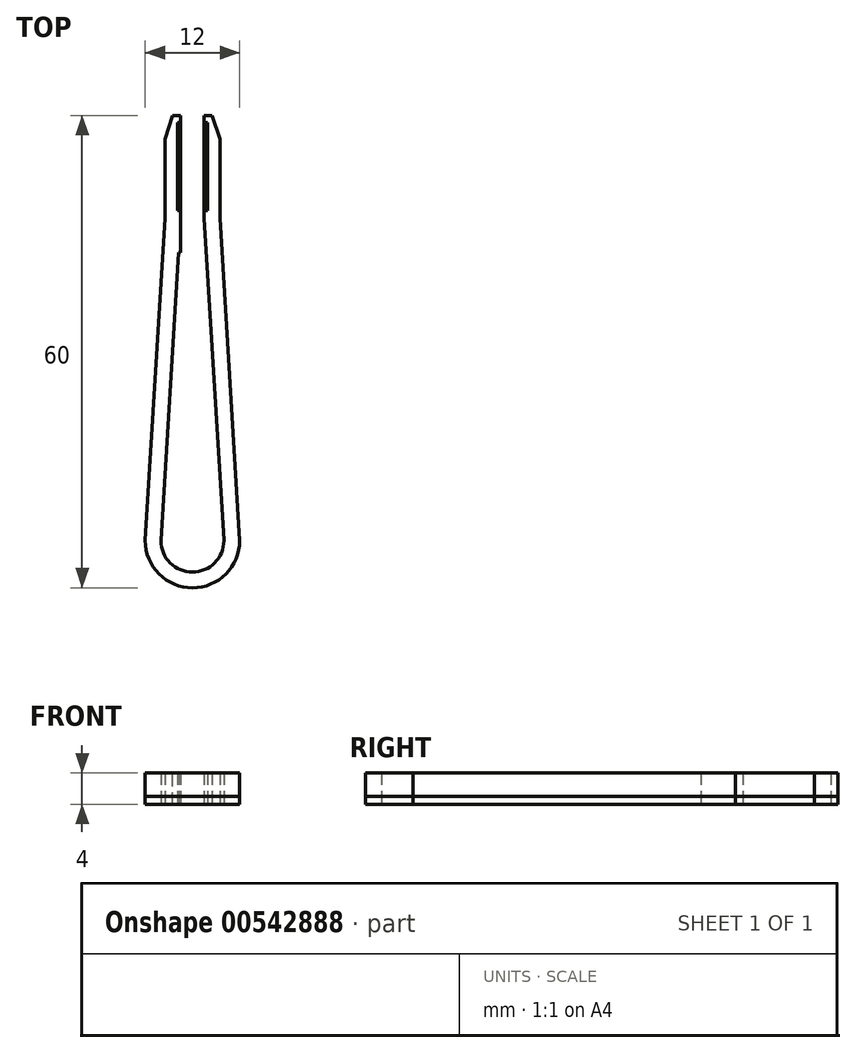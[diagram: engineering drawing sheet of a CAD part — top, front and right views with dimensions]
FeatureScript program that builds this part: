
annotation { "Feature Type Name" : "Feature", "Feature Type Description" : "" }
export const myFeature = defineFeature(function(context is Context, id is Id, definition is map)
    precondition{}
    {
        {
            var Q0;
            Q0=qCreatedBy(makeId("Top.planeOp"),FACE);
            var sketch = newSketch(context, id + "F0", { "sketchPlane" : qUnion([Q0])});
            skArc(sketch, "E0", {"start": v(-4, 0) * mm, "mid": v(0, -4) * mm, "end": v(4, 0) * mm});
            skArc(sketch, "E1", {"start": v(-6, 0) * mm, "mid": v(0, -6) * mm, "end": v(6, 0) * mm});
            skLineSegment(sketch, "E2.top", {"start": v(-1.5, 54) * mm, "end": v(-3.5, 54) * mm});
            skLineSegment(sketch, "E2.left", {"start": v(-1.5, 41.9) * mm, "end": v(-1.5, 54) * mm});
            skLineSegment(sketch, "E2.right", {"start": v(-3.5, 41) * mm, "end": v(-3.5, 54) * mm});
            skLineSegment(sketch, "E3.top", {"start": v(3.5, 54) * mm, "end": v(1.5, 54) * mm});
            skLineSegment(sketch, "E3.left", {"start": v(3.5, 41) * mm, "end": v(3.5, 54) * mm});
            skLineSegment(sketch, "E3.right", {"start": v(1.5, 41) * mm, "end": v(1.5, 54) * mm});
            skPoint(sketch, "E4", {"position": v(1.5, 47.5) * mm});
            skLineSegment(sketch, "E5.bottom", {"start": v(1.9, 53.1) * mm, "end": v(1.5, 53.1) * mm});
            skLineSegment(sketch, "E5.top", {"start": v(1.9, 41.9) * mm, "end": v(1.5, 41.9) * mm});
            skLineSegment(sketch, "E5.left", {"start": v(1.9, 53.1) * mm, "end": v(1.9, 41.9) * mm});
            skLineSegment(sketch, "E6", {"start": v(3.5, 41) * mm, "end": v(6, 0) * mm});
            skLineSegment(sketch, "E7", {"start": v(-3.5, 41) * mm, "end": v(-6, 0) * mm});
            skLineSegment(sketch, "E8", {"start": v(-1.77, 36.6) * mm, "end": v(-4, 0) * mm});
            skLineSegment(sketch, "E9", {"start": v(4, 0) * mm, "end": v(1.5, 41) * mm});
            skLineSegment(sketch, "E10.bottom", {"start": v(-1.5, 53.1) * mm, "end": v(-1.9, 53.1) * mm});
            skLineSegment(sketch, "E10.top", {"start": v(-1.5, 41.9) * mm, "end": v(-1.9, 41.9) * mm});
            skLineSegment(sketch, "E10.right", {"start": v(-1.9, 53.1) * mm, "end": v(-1.9, 41.9) * mm});
            skPoint(sketch, "E10.middle", {"position": v(-1.5, 47.3) * mm});
            skLineSegment(sketch, "E11", {"start": v(-1.5, 36.59) * mm, "end": v(-1.77, 36.6) * mm});
            skLineSegment(sketch, "E12", {"start": v(-1.5, 41.9) * mm, "end": v(-1.5, 36.59) * mm});
            skSolve(sketch);
        }
        {
            var Q0;
            Q0 = qSketchRegion(id + "F0", true);
            extrude(context, id + "F1", {"entities" : qUnion([Q0]), "depth" : 1 * mm, "offsetDistance" : 25 * mm});
        }
        {
            var Q0;
            Q0=makeQuery(id+"F0.imprint","IMPRINT",FACE,{"disambiguationData":[TD([[makeQuery(id+"F0.imprint","IMPRINT",EDGE,{"derivedFrom":sQuery(id+"F0.wireOp",EDGE,"E0")}),-1.0]])]});
            extrude(context, id + "F2", {"entities" : qUnion([Q0]), "depth" : 4 * mm, "offsetDistance" : 25 * mm});
        }
        {
            var Q0;
            Q0=makeQuery(id+"F2.opExtrude","SWEPT_EDGE",EDGE,{"disambiguationData":[OSD([sQuery(id+"F0.wireOp",EDGE,"E2.top"),sQuery(id+"F0.wireOp",EDGE,"E2.right")])]});
            var Q1;
            Q1=makeQuery(id+"F1.opExtrude","SWEPT_EDGE",EDGE,{"disambiguationData":[OSD([sQuery(id+"F0.wireOp",EDGE,"E2.top"),sQuery(id+"F0.wireOp",EDGE,"E2.right")])]});
            chamfer(context, id + "F3", {"entities" : qUnion([Q0, Q1]), "chamferType" : ChamferType.TWO_OFFSETS, "width1" : 3 * mm, "oppositeDirection" : false, "width2" : 1 * mm, "tangentPropagation" : true});
        }
        {
            var Q0;
            Q0=makeQuery(id+"F1.opExtrude","SWEPT_EDGE",EDGE,{"disambiguationData":[OSD([sQuery(id+"F0.wireOp",EDGE,"E3.top"),sQuery(id+"F0.wireOp",EDGE,"E3.left")])]});
            var Q1;
            Q1=makeQuery(id+"F2.opExtrude","SWEPT_EDGE",EDGE,{"disambiguationData":[OSD([sQuery(id+"F0.wireOp",EDGE,"E3.top"),sQuery(id+"F0.wireOp",EDGE,"E3.left")])]});
            chamfer(context, id + "F4", {"entities" : qUnion([Q0, Q1]), "chamferType" : ChamferType.TWO_OFFSETS, "width1" : 1 * mm, "oppositeDirection" : false, "width2" : 3 * mm, "tangentPropagation" : true});
        }
    });
